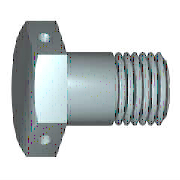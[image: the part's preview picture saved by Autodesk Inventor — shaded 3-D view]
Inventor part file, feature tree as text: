
AUTODESK INVENTOR PART (.ipt)
format: ipt  version: 2020 (Build 240168000, 168)  size: 214,528 bytes
history: native  units: mm (DEFAULTED — no unit token found)
features: sketch x4, extrude x2, other x1, chamfer x1, pattern_circular x1, plane x1
ambient origin geometry x7: Origin, YZ Plane, XZ Plane, X Axis, Y Axis, Z Axis, Center Point
bodies: Solid1 (feature_tree)
feature tree (10):
  other  "轴承体"
  extrude  "头"  Depth=30.0mm
  chamfer  "倒角1"  [1 undecoded]
  extrude  "孔"  TaperAngle=30.0deg  [1 undecoded]
  pattern_circular  "IDS_ARRAYHOLE"  Angle=90.0deg  [1 undecoded]
  plane  "Work Plane1"
  sketch  "草图1"  dims[d0=30.0mm d1=18.0mm]
  sketch  "草图2"  dims[d2=6.0mm]
  sketch  "草图3"  dims[d12=90.0deg]
  sketch  "草图4"  dims[d3=3.85mm d4=0.0mm d5=30.0deg d21=90.0deg d6=0.61345mm d7=0.61355mm d8=0.0mm d9=0.1501mm d10=8.9mm d11=10.0mm d13=0.61345mm d14=6.0mm d15=18.0mm d16=0.0mm d18=1.6mm d19=2.15mm d51=10.0mm d20=0.0mm d22=20.0mm d23=60.0deg d24=0.25mm d25=10.0mm d58=45.0deg d60=0.0mm d61=0.0mm]
note: 3 required parameter values undecoded (feature->parameter linkage not recoverable at this tier; creation-order binding heuristic only, values carry confidence <= 0.55)
